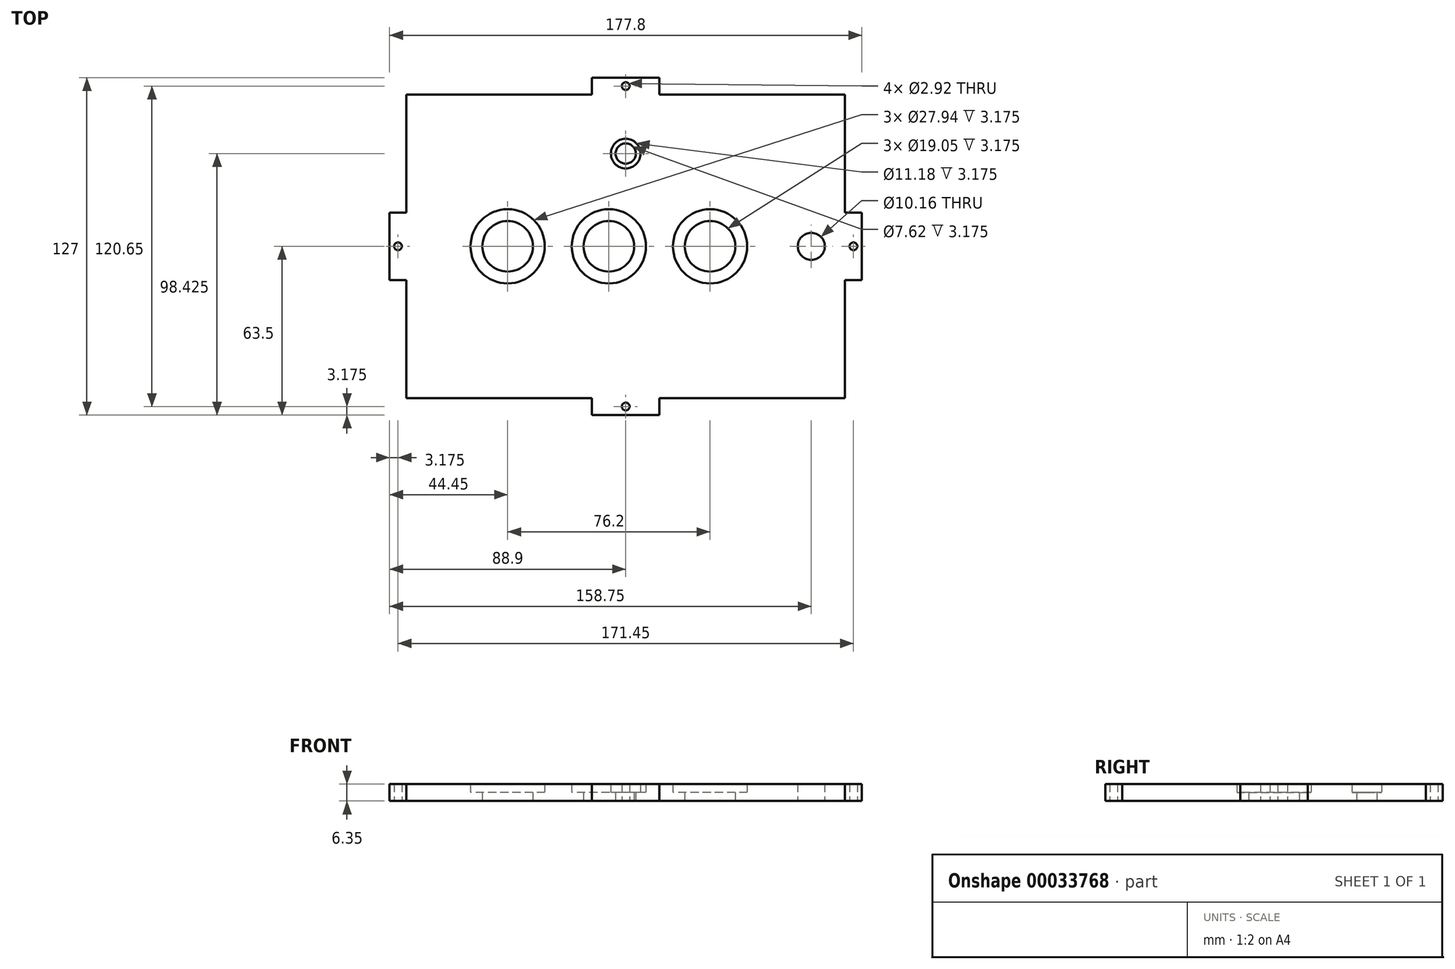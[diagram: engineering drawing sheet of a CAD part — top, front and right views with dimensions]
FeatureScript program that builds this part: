
annotation { "Feature Type Name" : "Feature", "Feature Type Description" : "" }
export const myFeature = defineFeature(function(context is Context, id is Id, definition is map)
    precondition{}
    {
        {
            var Q0;
            Q0=qCreatedBy(makeId("Top.planeOp"),FACE);
            var sketch = newSketch(context, id + "F0", { "sketchPlane" : qUnion([Q0])});
            skLineSegment(sketch, "E0.rect.bottom", {"start": v(12.7, -63.5) * mm, "end": v(-12.7, -63.5) * mm});
            skLineSegment(sketch, "E0.rect.left", {"start": v(88.9, -12.7) * mm, "end": v(88.9, 12.7) * mm});
            skLineSegment(sketch, "E0.rect.right", {"start": v(-88.9, -12.7) * mm, "end": v(-88.9, 12.7) * mm});
            skPoint(sketch, "E0.rect.middle", {"position": v(0, 0) * mm});
            skLineSegment(sketch, "E1", {"start": v(-88.9, 0) * mm, "end": v(-82.55, 0) * mm, "construction": true});
            skLineSegment(sketch, "E2", {"start": v(0, 63.5) * mm, "end": v(0, -63.5) * mm, "construction": true});
            skLineSegment(sketch, "E3.0", {"start": v(76.2, -63.5) * mm, "end": v(76.2, 63.5) * mm, "construction": true});
            skLineSegment(sketch, "E4.0", {"start": v(31.75, -63.5) * mm, "end": v(31.75, 63.5) * mm, "construction": true});
            skLineSegment(sketch, "E5.0", {"start": v(-6.35, -63.5) * mm, "end": v(-6.35, 63.5) * mm, "construction": true});
            skLineSegment(sketch, "E6.0", {"start": v(-44.45, -63.5) * mm, "end": v(-44.45, 63.5) * mm, "construction": true});
            skCircle(sketch, "E7", {"center": v(-44.45, 0) * mm, "radius": 9.53 * mm});
            skCircle(sketch, "E8", {"center": v(-44.45, 0) * mm, "radius": 13.97 * mm});
            skCircle(sketch, "E9", {"center": v(-6.35, 0) * mm, "radius": 9.53 * mm});
            skCircle(sketch, "E10", {"center": v(-6.35, 0) * mm, "radius": 13.97 * mm});
            skCircle(sketch, "E11", {"center": v(31.75, 0) * mm, "radius": 9.53 * mm});
            skCircle(sketch, "E12", {"center": v(31.75, 0) * mm, "radius": 13.97 * mm});
            skLineSegment(sketch, "E13.0", {"start": v(82.55, 57.15) * mm, "end": v(12.7, 57.15) * mm});
            skLineSegment(sketch, "E13.1", {"start": v(82.55, -57.15) * mm, "end": v(82.55, -12.7) * mm});
            skLineSegment(sketch, "E13.2", {"start": v(82.55, -57.15) * mm, "end": v(12.7, -57.15) * mm});
            skLineSegment(sketch, "E13.3", {"start": v(-82.55, -57.15) * mm, "end": v(-82.55, -12.7) * mm});
            skLineSegment(sketch, "E14.0", {"start": v(0, -63.5) * mm, "end": v(0, -57.15) * mm, "construction": true});
            skLineSegment(sketch, "E15.0", {"start": v(12.7, -63.5) * mm, "end": v(12.7, 63.5) * mm, "construction": true});
            skLineSegment(sketch, "E16.MirrorCS", {"start": v(-12.7, -63.5) * mm, "end": v(-12.7, 63.5) * mm, "construction": true});
            skLineSegment(sketch, "E17", {"start": v(-12.7, 63.5) * mm, "end": v(-12.7, 57.15) * mm});
            skLineSegment(sketch, "E18", {"start": v(12.7, 63.5) * mm, "end": v(12.7, 57.15) * mm});
            skLineSegment(sketch, "E19.trimOffspring", {"start": v(-12.7, 57.15) * mm, "end": v(-82.55, 57.15) * mm});
            skLineSegment(sketch, "E20.MirrorCS", {"start": v(-12.7, -63.5) * mm, "end": v(-12.7, -57.15) * mm});
            skLineSegment(sketch, "E21.MirrorCS", {"start": v(12.7, -63.5) * mm, "end": v(12.7, -57.15) * mm});
            skLineSegment(sketch, "E22.trimOffspring", {"start": v(-12.7, -57.15) * mm, "end": v(-82.55, -57.15) * mm});
            skLineSegment(sketch, "E23", {"start": v(-12.7, -57.15) * mm, "end": v(0, -57.15) * mm, "construction": true});
            skLineSegment(sketch, "E24", {"start": v(0, -57.15) * mm, "end": v(12.7, -57.15) * mm, "construction": true});
            skLineSegment(sketch, "E25", {"start": v(0, -57.15) * mm, "end": v(0, 63.5) * mm, "construction": true});
            skCircle(sketch, "E26", {"center": v(0, -60.32) * mm, "radius": 1.46 * mm});
            skCircle(sketch, "E27.MirrorC", {"center": v(0, 60.32) * mm, "radius": 1.46 * mm});
            skLineSegment(sketch, "E28.0", {"start": v(-88.9, -12.7) * mm, "end": v(88.9, -12.7) * mm, "construction": true});
            skLineSegment(sketch, "E29.MirrorCS", {"start": v(-88.9, 12.7) * mm, "end": v(88.9, 12.7) * mm, "construction": true});
            skLineSegment(sketch, "E30", {"start": v(-88.9, 12.7) * mm, "end": v(-82.55, 12.7) * mm});
            skLineSegment(sketch, "E31", {"start": v(-88.9, -12.7) * mm, "end": v(-82.55, -12.7) * mm});
            skLineSegment(sketch, "E32.trimOffspring", {"start": v(-82.55, 12.7) * mm, "end": v(-82.55, 57.15) * mm});
            skLineSegment(sketch, "E33", {"start": v(-82.55, 12.7) * mm, "end": v(-82.55, 0) * mm, "construction": true});
            skLineSegment(sketch, "E34", {"start": v(-82.55, 0) * mm, "end": v(-82.55, -12.7) * mm, "construction": true});
            skLineSegment(sketch, "E35", {"start": v(-82.55, 0) * mm, "end": v(88.9, 0) * mm, "construction": true});
            skCircle(sketch, "E36", {"center": v(-85.72, 0) * mm, "radius": 1.46 * mm});
            skLineSegment(sketch, "E37.MirrorCS", {"start": v(88.9, -12.7) * mm, "end": v(82.55, -12.7) * mm});
            skLineSegment(sketch, "E38.MirrorCS", {"start": v(88.9, 12.7) * mm, "end": v(82.55, 12.7) * mm});
            skCircle(sketch, "E39.MirrorC", {"center": v(85.72, 0) * mm, "radius": 1.46 * mm});
            skLineSegment(sketch, "E40.trimOffspring", {"start": v(82.55, 12.7) * mm, "end": v(82.55, 57.15) * mm});
            skPoint(sketch, "E41.orphan", {"position": v(-88.9, 63.5) * mm});
            skLineSegment(sketch, "E42.trimOffspring", {"start": v(12.7, 63.5) * mm, "end": v(-12.7, 63.5) * mm});
            skPoint(sketch, "E43.orphan", {"position": v(88.9, 63.5) * mm});
            skPoint(sketch, "E44.orphan", {"position": v(88.9, -63.5) * mm});
            skPoint(sketch, "E45.orphan", {"position": v(-88.9, -63.5) * mm});
            skLineSegment(sketch, "E46", {"start": v(-82.55, 34.92) * mm, "end": v(0, 34.92) * mm, "construction": true});
            skCircle(sketch, "E47", {"center": v(0, 34.92) * mm, "radius": 3.81 * mm});
            skCircle(sketch, "E48", {"center": v(0, 34.92) * mm, "radius": 5.59 * mm});
            skLineSegment(sketch, "E49.0", {"start": v(69.85, -63.5) * mm, "end": v(69.85, 63.5) * mm, "construction": true});
            skCircle(sketch, "E50", {"center": v(69.85, 0) * mm, "radius": 5.08 * mm});
            skLineSegment(sketch, "E51", {"start": v(-122.41, -26.02) * mm, "end": v(-85.82, -102.45) * mm, "construction": true});
            skLineSegment(sketch, "E52", {"start": v(-85.82, -102.45) * mm, "end": v(-49.47, -143.82) * mm, "construction": true});
            skLineSegment(sketch, "E53", {"start": v(-48.89, -143.45) * mm, "end": v(-52.9, -97.97) * mm, "construction": true});
            skLineSegment(sketch, "E54", {"start": v(-52.9, -97.97) * mm, "end": v(-122.41, -26.02) * mm, "construction": true});
            skSolve(sketch);
        }
        {
            var Q0;
            Q0=makeQuery(id+"F0.imprint","IMPRINT",FACE,{"disambiguationData":[TD([[makeQuery(id+"F0.imprint","IMPRINT",EDGE,{"derivedFrom":sQuery(id+"F0.wireOp",EDGE,"E0.rect.bottom")}),-1.0]])]});
            extrude(context, id + "F1", {"entities" : qUnion([Q0]), "depth" : 6.35 * mm});
        }
        {
            var Q0;
            Q0=makeQuery(id+"F0.imprint","IMPRINT",FACE,{"disambiguationData":[TD([[makeQuery(id+"F0.imprint","IMPRINT",EDGE,{"derivedFrom":sQuery(id+"F0.wireOp",EDGE,"E7")}),-1.0]])]});
            var Q1;
            Q1=makeQuery(id+"F0.imprint","IMPRINT",FACE,{"disambiguationData":[TD([[makeQuery(id+"F0.imprint","IMPRINT",EDGE,{"derivedFrom":sQuery(id+"F0.wireOp",EDGE,"E9")}),-1.0]])]});
            var Q2;
            Q2=makeQuery(id+"F0.imprint","IMPRINT",FACE,{"disambiguationData":[TD([[makeQuery(id+"F0.imprint","IMPRINT",EDGE,{"derivedFrom":sQuery(id+"F0.wireOp",EDGE,"E11")}),-1.0]])]});
            extrude(context, id + "F2", {"entities" : qUnion([Q0, Q1, Q2]), "operationType" : NewBodyOperationType.ADD, "depth" : 3.17 * mm});
        }
        {
            var Q0;
            Q0=makeQuery(id+"F0.imprint","IMPRINT",FACE,{"disambiguationData":[TD([[makeQuery(id+"F0.imprint","IMPRINT",EDGE,{"derivedFrom":sQuery(id+"F0.wireOp",EDGE,"E47")}),-1.0]])]});
            extrude(context, id + "F3", {"entities" : qUnion([Q0]), "operationType" : NewBodyOperationType.ADD, "depth" : 3.17 * mm});
        }
    });
